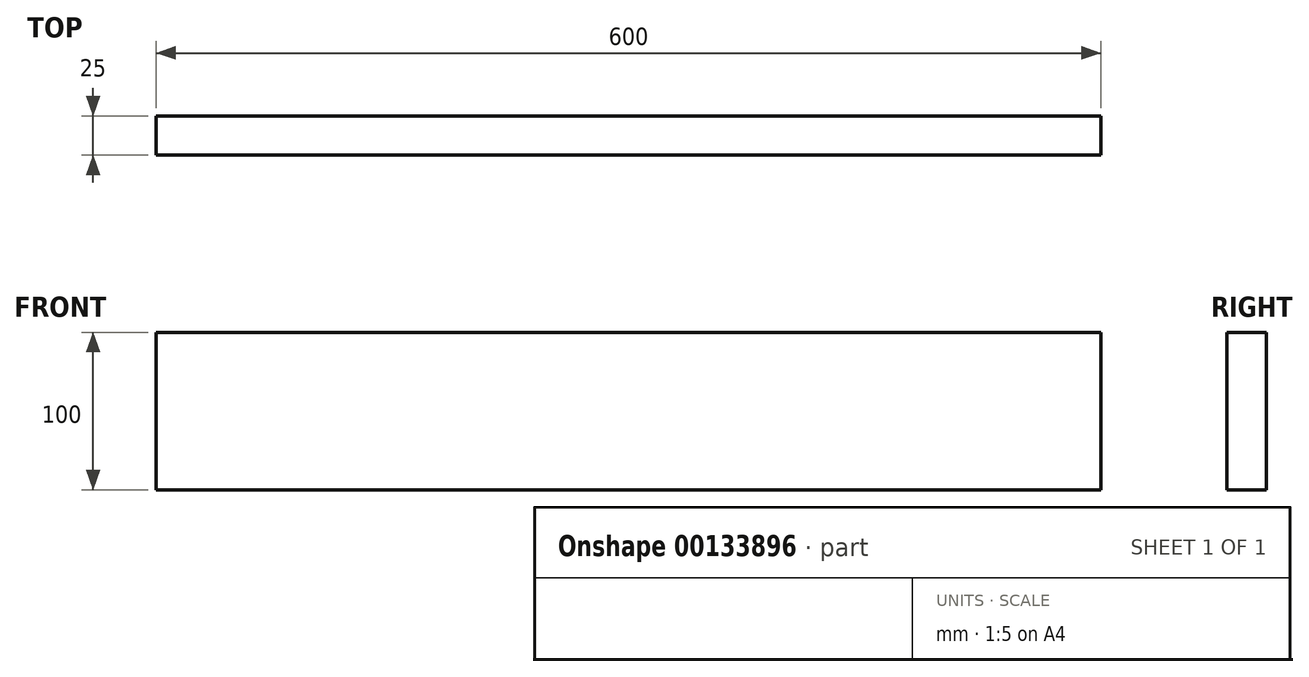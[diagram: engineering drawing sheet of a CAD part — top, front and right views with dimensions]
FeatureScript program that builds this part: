
annotation { "Feature Type Name" : "Feature", "Feature Type Description" : "" }
export const myFeature = defineFeature(function(context is Context, id is Id, definition is map)
    precondition{}
    {
        {
            var Q0;
            Q0=qCreatedBy(makeId("Front.planeOp"),FACE);
            var sketch = newSketch(context, id + "F0", { "sketchPlane" : qUnion([Q0])});
            skLineSegment(sketch, "E0.bottom", {"start": v(300, -39) * mm, "end": v(-300, -39) * mm});
            skLineSegment(sketch, "E0.top", {"start": v(300, 61) * mm, "end": v(-300, 61) * mm});
            skLineSegment(sketch, "E0.left", {"start": v(300, -39) * mm, "end": v(300, 61) * mm});
            skLineSegment(sketch, "E0.right", {"start": v(-300, -39) * mm, "end": v(-300, 61) * mm});
            skPoint(sketch, "E0.middle", {"position": v(0, 11) * mm});
            skSolve(sketch);
        }
        {
            var Q0;
            Q0=makeQuery(id+"F0.imprint","IMPRINT",FACE,{"disambiguationData":[TD([[makeQuery(id+"F0.imprint","IMPRINT",EDGE,{"derivedFrom":sQuery(id+"F0.wireOp",EDGE,"E0.bottom")}),-1.0]])]});
            extrude(context, id + "F1", {"entities" : qUnion([Q0]), "depth" : 25 * mm});
        }
    });
